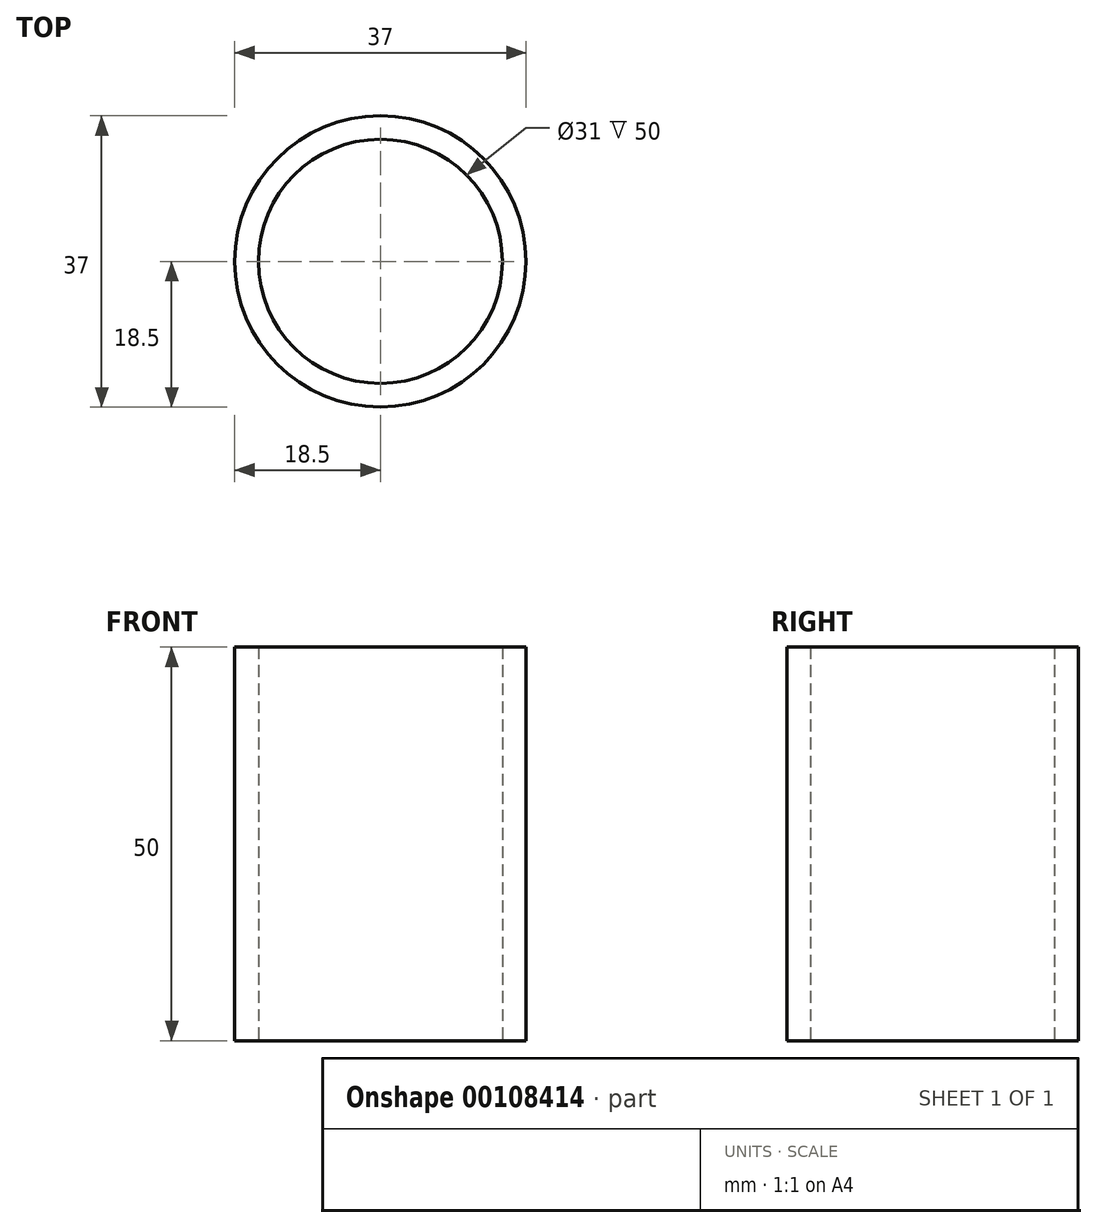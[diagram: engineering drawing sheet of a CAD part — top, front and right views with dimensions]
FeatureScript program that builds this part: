
annotation { "Feature Type Name" : "Feature", "Feature Type Description" : "" }
export const myFeature = defineFeature(function(context is Context, id is Id, definition is map)
    precondition{}
    {
        {
            var Q0;
            Q0=qCreatedBy(makeId("Top.planeOp"),FACE);
            var sketch = newSketch(context, id + "F0", { "sketchPlane" : qUnion([Q0])});
            skCircle(sketch, "E0", {"center": v(0, 0) * mm, "radius": 15.5 * mm});
            skCircle(sketch, "E1", {"center": v(0, 0) * mm, "radius": 18.5 * mm});
            skSolve(sketch);
        }
        {
            var Q0;
            Q0=makeQuery(id+"F0.imprint","IMPRINT",FACE,{"disambiguationData":[TD([[makeQuery(id+"F0.imprint","IMPRINT",EDGE,{"derivedFrom":sQuery(id+"F0.wireOp",EDGE,"E0")}),-1.0]])]});
            extrude(context, id + "F1", {"entities" : qUnion([Q0]), "depth" : 50 * mm});
        }
    });
